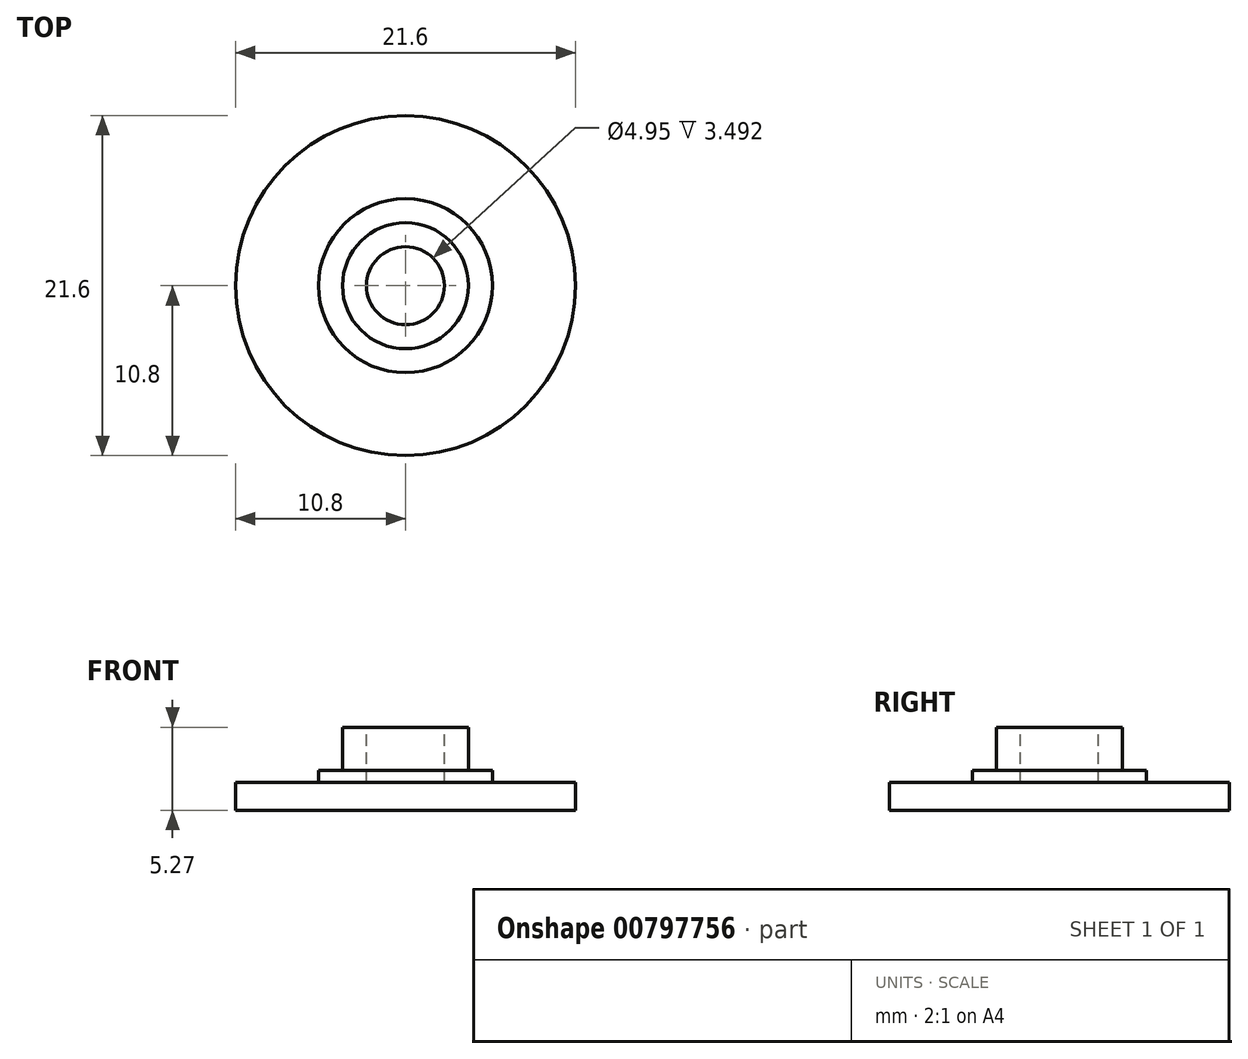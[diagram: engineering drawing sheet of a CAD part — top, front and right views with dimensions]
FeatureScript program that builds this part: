
annotation { "Feature Type Name" : "Feature", "Feature Type Description" : "" }
export const myFeature = defineFeature(function(context is Context, id is Id, definition is map)
    precondition{}
    {
        {
            var Q0;
            Q0=qCreatedBy(makeId("Front.planeOp"),FACE);
            var sketch = newSketch(context, id + "F0", { "sketchPlane" : qUnion([Q0])});
            skLineSegment(sketch, "E0", {"start": v(0, 0) * mm, "end": v(10.8, 0) * mm});
            skLineSegment(sketch, "E1", {"start": v(10.8, 0) * mm, "end": v(10.8, 1.78) * mm});
            skLineSegment(sketch, "E2", {"start": v(10.8, 1.78) * mm, "end": v(4, 1.78) * mm});
            skLineSegment(sketch, "E3", {"start": v(4, 1.78) * mm, "end": v(4, 5.27) * mm});
            skLineSegment(sketch, "E4", {"start": v(4, 5.27) * mm, "end": v(2.48, 5.27) * mm});
            skLineSegment(sketch, "E5", {"start": v(2.48, 5.27) * mm, "end": v(2.48, 1.78) * mm});
            skLineSegment(sketch, "E6", {"start": v(2.48, 1.78) * mm, "end": v(0, 1.78) * mm});
            skLineSegment(sketch, "E7", {"start": v(0, 1.78) * mm, "end": v(0, 0) * mm});
            skLineSegment(sketch, "E8", {"start": v(0, 26.63) * mm, "end": v(0, 0) * mm, "construction": true});
            skLineSegment(sketch, "E9", {"start": v(5.52, 1.78) * mm, "end": v(5.52, 2.54) * mm});
            skLineSegment(sketch, "E10", {"start": v(5.52, 2.54) * mm, "end": v(4, 2.54) * mm});
            skSolve(sketch);
        }
        {
            var Q0;
            Q0=makeQuery(id+"F0.imprint","IMPRINT",FACE,{"disambiguationData":[TD([[makeQuery(id+"F0.imprint","IMPRINT",EDGE,{"derivedFrom":sQuery(id+"F0.wireOp",EDGE,"E0")}),1.0]])]});
            var Q1;
            {var subQ3=sQuery(id+"F0.wireOp",EDGE,"E9");Q1=makeQuery(id+"F0.imprint","IMPRINT",FACE,{"disambiguationData":[TD([[makeQuery(id+"F0.imprint","IMPRINT",EDGE,{"derivedFrom":subQ3}),1.0]])]});}
            var Q2;
            Q2=sQuery(id+"F0.wireOp",EDGE,"E8");
            revolve(context, id + "F1", {"surfaceOperationType" : NewSurfaceOperationType.NEW, "entities" : qUnion([Q0, Q1]), "axis" : qUnion([Q2]), "revolveType" : RevolveType.FULL});
        }
    });
